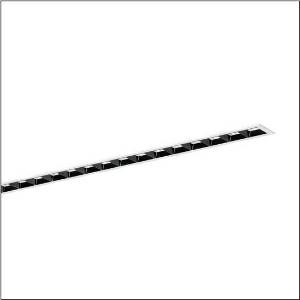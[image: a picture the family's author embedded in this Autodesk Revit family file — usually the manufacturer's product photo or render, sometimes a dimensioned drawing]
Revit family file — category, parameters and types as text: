
# Revit family: silica_r__21_51mx11tbt5w_4029
name_source: partatom
category: Lighting Fixtures
units: mm (PartAtom-declared; Revit-internal decimal feet)

## family parameters
Cut with Voids When Loaded = No
Host = Face
Light Source = No
Part Type = Normal
Room Calculation Point = No
Round Connector Dimension = Use Diameter
Shared = No

## types (1)
- --- (1 x LED, 4650 lm, 40.3 W, 6500K)
    Apparent Load = 40 VA
    CIE Flux Codes = 85 99 100 100 100
    Color Rendering = 80
    Color Temperature = 6500K
    Default Elevation = 1800 mm
    Description = Silica® 21, office luminaire, primary light control with darklight reflector, of PMMA, black, CAT 2 (L<= 3000cd/m²), light emission: direct distribution, primary light characteristic: symmetric, installation type: recessed, LED, rated luminous flux: 4.650lm, luminous efficacy: 110lm/W, light colour: 8tw, colour temperature: 2700..6500K, control gear: DALI DT8, with terminal, 3+2-pole, max. 2.5mm², mains connection: 220..240V, AC, 50/60Hz, rated input power: 42.3W, luminaire housing, of aluminium, traffic white (RAL 9016), length: 1.528mm, width: 79mm, height: 53mm, protection rating (complete): IP20, insulation class (complete): insulation class I (protective earthing), certification: CE, ENEC, VDE, permissible operating ambient temperature: 0..+35°C, standard: EN 50419, packaging unit: 1 piece
    Height = 0 mm  [stored 0 ft]
    Lamp = 1 x LED
    Lamp Light Flux = 4650 lm
    Lamp Power = 40.3 W
    Lamp count = 1
    Length = 1527 mm
    Luminous efficacy = 115 lm/W
    Manufacturer = Siteco
    ModVariant = No
    Model = 51MX11TBT5W
    Mounting Place = Ceiling
    Mounting Type = Recessed
    Number of Poles = 1
    OnlyDefault = Yes
    Power Factor = 1
    Product Name = Silica® 21
    Product group = office luminaire | ceiling recessed
    ProductGroupID = 401
    Protection Class = Protection class I
    Protection Degree = IP 20
    RLX_Detail_Level = 1
    RLX_Emergency_Light_Flux = 0 lm
    RLX_Emergency_Type = 0
    RLX_Emergency_Type_DB = No
    RlxData = <blob elided: 38921 chars, md5=626ac16a>
    Socket = socket
    Standby Power = 0 W
    System Light Flux = 4650 lm
    System Power = 40 W
    Type Comments = individual setting
    Type Image = l_1335880.jpg
    URL = http://relux.com
    VarID = @adj_140100
    Voltage = 0 V
    Weight = 0.00 kg
    Width = 79 mm

note: [stored X ft] marks values corroborated as IEEE doubles in the binary element streams (Revit-internal decimal feet)

## geometry (parser evidence)
native form markers: Blend x4, Sweep x9
no freeform markers — native parametric forms only
